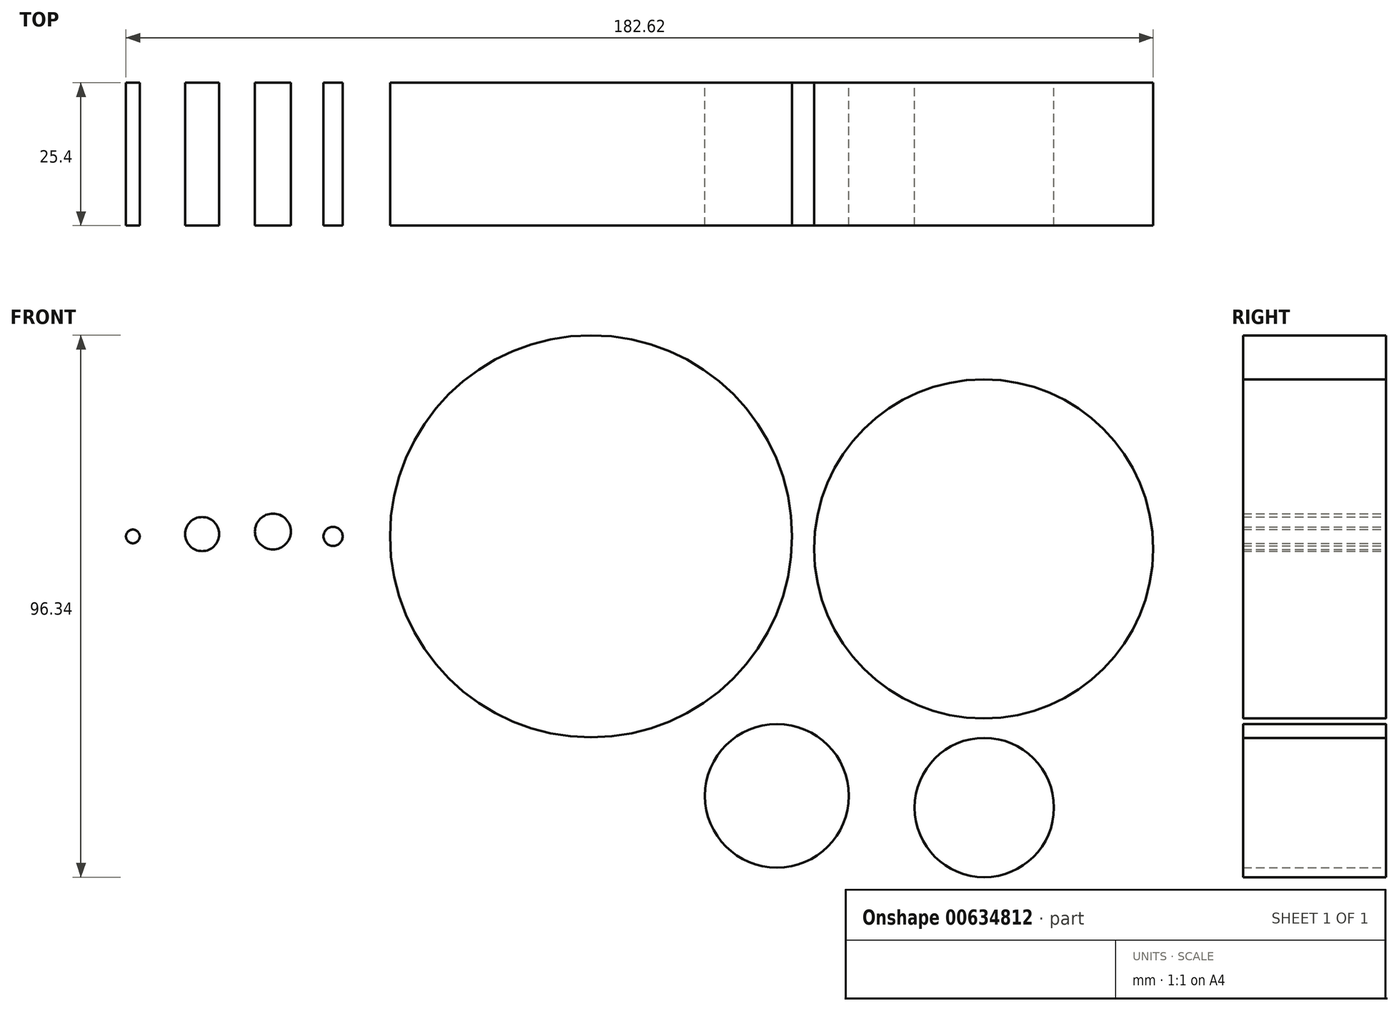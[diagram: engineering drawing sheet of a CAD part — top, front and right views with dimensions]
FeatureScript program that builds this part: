
annotation { "Feature Type Name" : "Feature", "Feature Type Description" : "" }
export const myFeature = defineFeature(function(context is Context, id is Id, definition is map)
    precondition{}
    {
        {
            var Q0;
            Q0=qCreatedBy(makeId("Front.planeOp"),FACE);
            var sketch = newSketch(context, id + "F0", { "sketchPlane" : qUnion([Q0])});
            skCircle(sketch, "E0", {"center": v(0, 0) * mm, "radius": 35.75 * mm});
            skCircle(sketch, "E1", {"center": v(-81.47, 0) * mm, "radius": 1.22 * mm});
            skCircle(sketch, "E2", {"center": v(-69.15, 0.4) * mm, "radius": 3.03 * mm});
            skCircle(sketch, "E3", {"center": v(-56.57, 0.87) * mm, "radius": 3.19 * mm});
            skCircle(sketch, "E4", {"center": v(-45.87, 0) * mm, "radius": 1.7 * mm});
            skCircle(sketch, "E5", {"center": v(69.8, -2.23) * mm, "radius": 30.13 * mm});
            skCircle(sketch, "E6", {"center": v(33.03, -46.14) * mm, "radius": 12.78 * mm});
            skCircle(sketch, "E7", {"center": v(69.9, -48.21) * mm, "radius": 12.38 * mm});
            skSolve(sketch);
        }
        {
            var Q0;
            Q0=makeQuery(id+"F0.imprint","IMPRINT",FACE,{"disambiguationData":[TD([[makeQuery(id+"F0.imprint","IMPRINT",EDGE,{"derivedFrom":sQuery(id+"F0.wireOp",EDGE,"E1")}),1.0]])]});
            var Q1;
            Q1=makeQuery(id+"F0.imprint","IMPRINT",FACE,{"disambiguationData":[TD([[makeQuery(id+"F0.imprint","IMPRINT",EDGE,{"derivedFrom":sQuery(id+"F0.wireOp",EDGE,"E2")}),1.0]])]});
            var Q2;
            Q2=makeQuery(id+"F0.imprint","IMPRINT",FACE,{"disambiguationData":[TD([[makeQuery(id+"F0.imprint","IMPRINT",EDGE,{"derivedFrom":sQuery(id+"F0.wireOp",EDGE,"E3")}),1.0]])]});
            var Q3;
            Q3=makeQuery(id+"F0.imprint","IMPRINT",FACE,{"disambiguationData":[TD([[makeQuery(id+"F0.imprint","IMPRINT",EDGE,{"derivedFrom":sQuery(id+"F0.wireOp",EDGE,"E4")}),1.0]])]});
            var Q4;
            Q4=makeQuery(id+"F0.imprint","IMPRINT",FACE,{"disambiguationData":[TD([[makeQuery(id+"F0.imprint","IMPRINT",EDGE,{"derivedFrom":sQuery(id+"F0.wireOp",EDGE,"E0")}),1.0]])]});
            var Q5;
            Q5=makeQuery(id+"F0.imprint","IMPRINT",FACE,{"disambiguationData":[TD([[makeQuery(id+"F0.imprint","IMPRINT",EDGE,{"derivedFrom":sQuery(id+"F0.wireOp",EDGE,"E5")}),1.0]])]});
            var Q6;
            Q6=makeQuery(id+"F0.imprint","IMPRINT",FACE,{"disambiguationData":[TD([[makeQuery(id+"F0.imprint","IMPRINT",EDGE,{"derivedFrom":sQuery(id+"F0.wireOp",EDGE,"E6")}),1.0]])]});
            var Q7;
            Q7=makeQuery(id+"F0.imprint","IMPRINT",FACE,{"disambiguationData":[TD([[makeQuery(id+"F0.imprint","IMPRINT",EDGE,{"derivedFrom":sQuery(id+"F0.wireOp",EDGE,"E7")}),1.0]])]});
            extrude(context, id + "F1", {"entities" : qUnion([Q0, Q1, Q2, Q3, Q4, Q5, Q6, Q7]), "depth" : 25.4 * mm, "offsetDistance" : 25.4 * mm});
        }
    });
